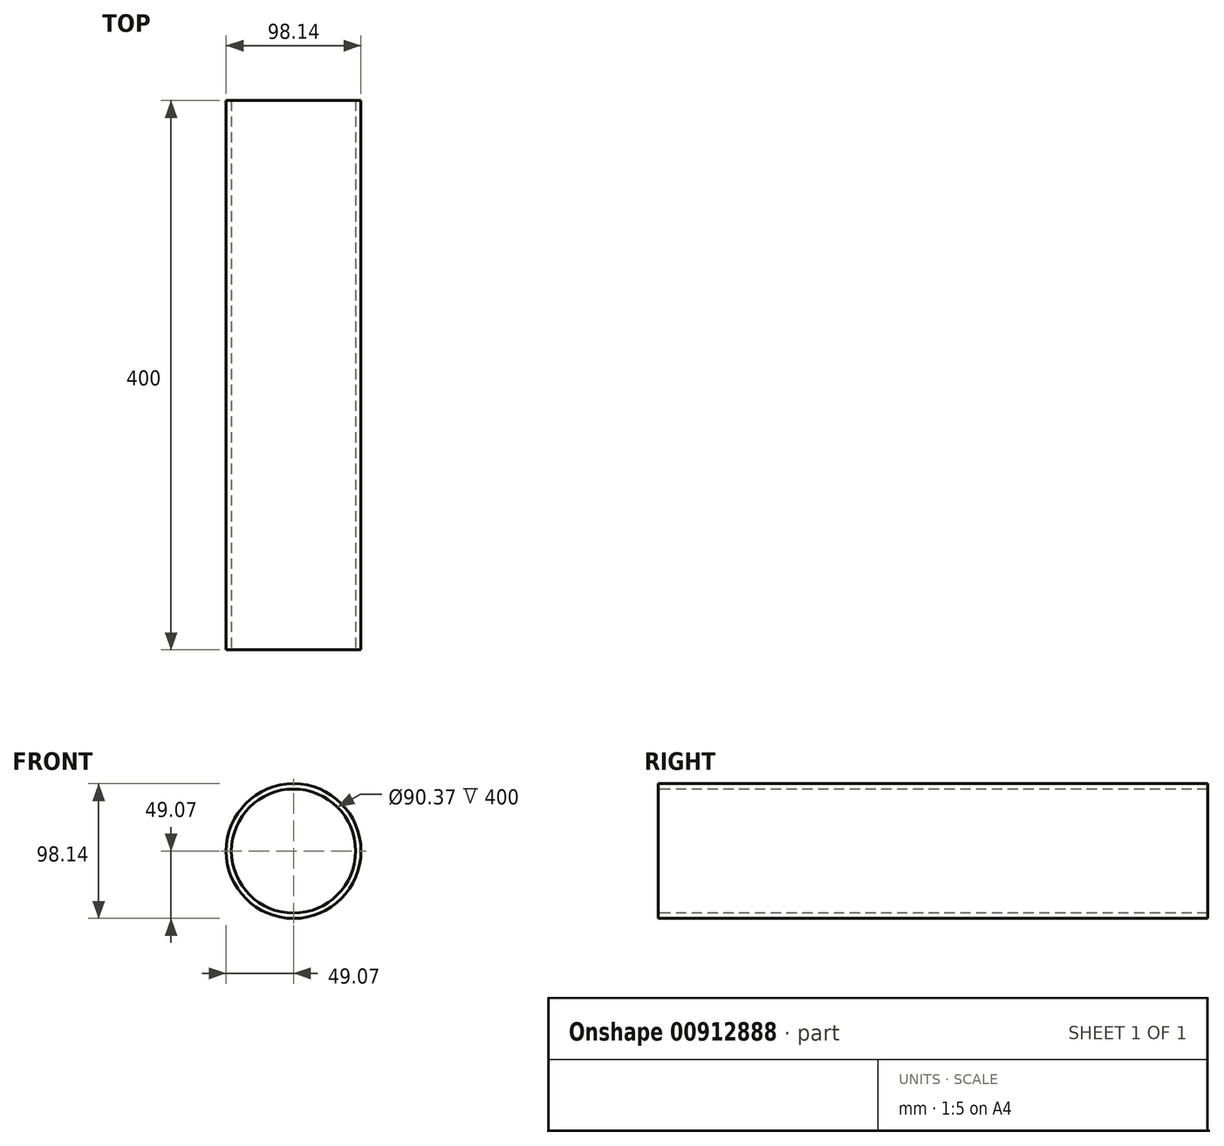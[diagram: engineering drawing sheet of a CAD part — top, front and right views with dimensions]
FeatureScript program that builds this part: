
annotation { "Feature Type Name" : "Feature", "Feature Type Description" : "" }
export const myFeature = defineFeature(function(context is Context, id is Id, definition is map)
    precondition{}
    {
        {
            var Q0;
            Q0=qCreatedBy(makeId("Front.planeOp"),FACE);
            var sketch = newSketch(context, id + "F0", { "sketchPlane" : qUnion([Q0])});
            skCircle(sketch, "E0", {"center": v(0, 0) * mm, "radius": 49.07 * mm});
            skSolve(sketch);
        }
        {
            var Q0;
            Q0=makeQuery(id+"F0.imprint","IMPRINT",FACE,{"disambiguationData":[TD([[makeQuery(id+"F0.imprint","IMPRINT",EDGE,{"derivedFrom":sQuery(id+"F0.wireOp",EDGE,"E0")}),1.0]])]});
            extrude(context, id + "F1", {"entities" : qUnion([Q0]), "oppositeDirection" : true, "depth" : 400 * mm, "offsetDistance" : 25.4 * mm});
        }
        {
            var Q0;
            Q0=makeQuery(id+"F1.opExtrude","CAP_FACE",FACE,{"disambiguationData":[OSD([sQuery(id+"F0.wireOp",EDGE,"E0")])],"isStart":false});
            var sketch = newSketch(context, id + "F2", { "sketchPlane" : qUnion([Q0])});
            skCircle(sketch, "E1", {"center": v(0, 0) * mm, "radius": 45.18 * mm});
            skSolve(sketch);
        }
        {
            var Q0;
            Q0=makeQuery(id+"F2.imprint","IMPRINT",FACE,{"disambiguationData":[TD([[makeQuery(id+"F2.imprint","IMPRINT",EDGE,{"derivedFrom":sQuery(id+"F2.wireOp",EDGE,"E1")}),1.0]])]});
            extrude(context, id + "F3", {"entities" : qUnion([Q0]), "operationType" : NewBodyOperationType.ADD, "oppositeDirection" : true, "depth" : 408.94 * mm, "offsetDistance" : 25.4 * mm});
        }
        {
            var Q0;
            Q0=makeQuery(id+"F3.opExtrude","CAP_FACE",FACE,{"disambiguationData":[OSD([sQuery(id+"F2.wireOp",EDGE,"E1")])],"isStart":false});
            extrude(context, id + "F4", {"entities" : qUnion([Q0]), "operationType" : NewBodyOperationType.REMOVE, "oppositeDirection" : true, "depth" : 500.38 * mm, "offsetDistance" : 25.4 * mm});
        }
    });
